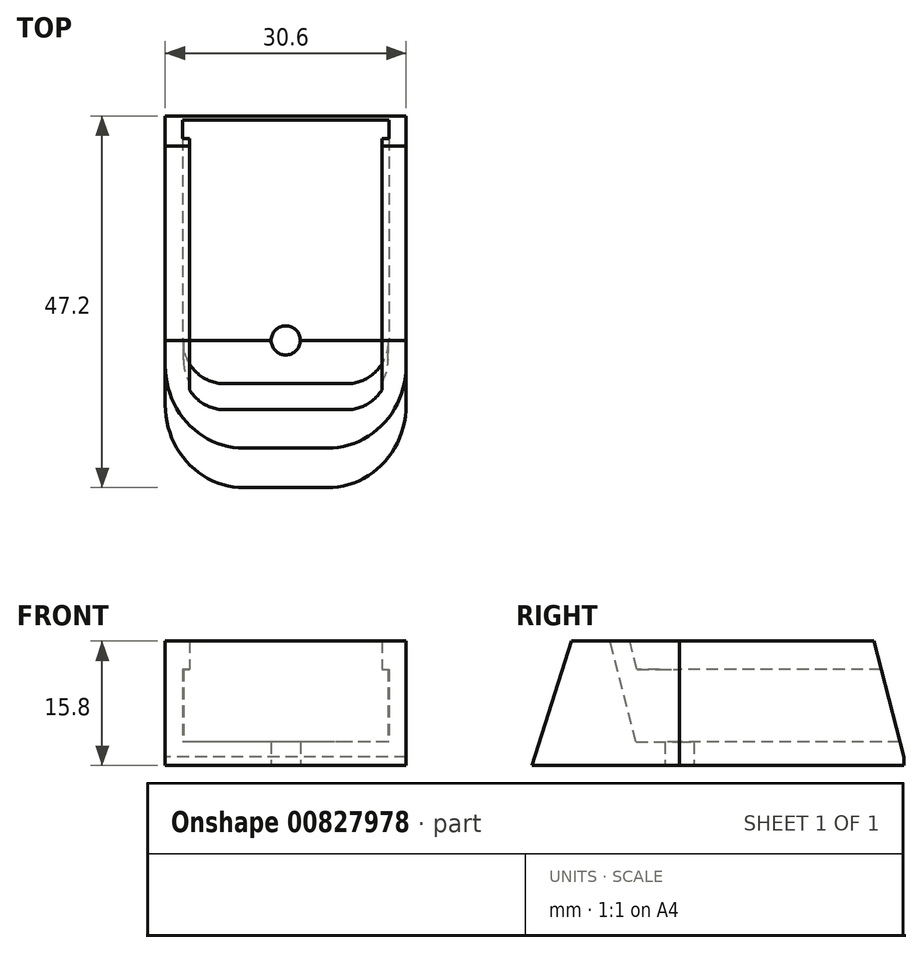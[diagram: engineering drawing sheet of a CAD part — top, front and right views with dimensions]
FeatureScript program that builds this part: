
annotation { "Feature Type Name" : "Feature", "Feature Type Description" : "" }
export const myFeature = defineFeature(function(context is Context, id is Id, definition is map)
    precondition{}
    {
        {
            var Q0;
            Q0=qCreatedBy(makeId("Front.planeOp"),FACE);
            var sketch = newSketch(context, id + "F0", { "sketchPlane" : qUnion([Q0])});
            skLineSegment(sketch, "E0", {"start": v(0, 0) * mm, "end": v(15.3, 0) * mm});
            skLineSegment(sketch, "E1", {"start": v(15.3, 0) * mm, "end": v(15.3, 15.8) * mm});
            skLineSegment(sketch, "E2", {"start": v(15.3, 15.8) * mm, "end": v(12.2, 15.8) * mm});
            skLineSegment(sketch, "E3", {"start": v(12.2, 15.8) * mm, "end": v(12.2, 12.2) * mm});
            skLineSegment(sketch, "E4", {"start": v(12.2, 12.2) * mm, "end": v(13.1, 12.2) * mm});
            skLineSegment(sketch, "E5", {"start": v(13.1, 12.2) * mm, "end": v(13.1, 3) * mm});
            skLineSegment(sketch, "E6", {"start": v(13.1, 3) * mm, "end": v(0, 3) * mm});
            skLineSegment(sketch, "E7", {"start": v(0, 0) * mm, "end": v(0, 34.13) * mm, "construction": true});
            skLineSegment(sketch, "E8.MirrorCS", {"start": v(-13.1, 3) * mm, "end": v(0, 3) * mm});
            skLineSegment(sketch, "E9.MirrorCS", {"start": v(0, 0) * mm, "end": v(-15.3, 0) * mm});
            skLineSegment(sketch, "E10.MirrorCS", {"start": v(-15.3, 0) * mm, "end": v(-15.3, 15.8) * mm});
            skLineSegment(sketch, "E11.MirrorCS", {"start": v(-13.1, 12.2) * mm, "end": v(-13.1, 3) * mm});
            skLineSegment(sketch, "E12.MirrorCS", {"start": v(-12.2, 12.2) * mm, "end": v(-13.1, 12.2) * mm});
            skLineSegment(sketch, "E13.MirrorCS", {"start": v(-15.3, 15.8) * mm, "end": v(-12.2, 15.8) * mm});
            skLineSegment(sketch, "E14.MirrorCS", {"start": v(-12.2, 15.8) * mm, "end": v(-12.2, 12.2) * mm});
            skSolve(sketch);
        }
        {
            var Q0;
            Q0=qCreatedBy(makeId("Right.planeOp"),FACE);
            var sketch = newSketch(context, id + "F1", { "sketchPlane" : qUnion([Q0])});
            skLineSegment(sketch, "E15", {"start": v(0, 0) * mm, "end": v(-18.7, 0) * mm});
            skLineSegment(sketch, "E16", {"start": v(-18.7, 0) * mm, "end": v(-13.7, 15.8) * mm});
            skLineSegment(sketch, "E17", {"start": v(-13.7, 15.8) * mm, "end": v(0, 15.8) * mm});
            skLineSegment(sketch, "E18", {"start": v(0, 15.8) * mm, "end": v(0, 0) * mm});
            skSolve(sketch);
        }
        {
            var Q0;
            Q0=qCreatedBy(makeId("Right.planeOp"),FACE);
            var sketch = newSketch(context, id + "F2", { "sketchPlane" : qUnion([Q0])});
            skLineSegment(sketch, "E19", {"start": v(0, 0) * mm, "end": v(0, 3) * mm, "construction": true});
            skLineSegment(sketch, "E20", {"start": v(0, 3) * mm, "end": v(-5.5, 3) * mm});
            skLineSegment(sketch, "E21", {"start": v(-5.5, 3) * mm, "end": v(-7.87, 12.2) * mm});
            skLineSegment(sketch, "E22", {"start": v(-7.87, 12.2) * mm, "end": v(25.63, 12.2) * mm});
            skLineSegment(sketch, "E23", {"start": v(25.63, 12.2) * mm, "end": v(28, 3) * mm});
            skLineSegment(sketch, "E24", {"start": v(28, 3) * mm, "end": v(0, 3) * mm});
            skLineSegment(sketch, "E25", {"start": v(-7.87, 12.2) * mm, "end": v(-8.8, 15.8) * mm});
            skLineSegment(sketch, "E26", {"start": v(-8.8, 15.8) * mm, "end": v(24.7, 15.8) * mm});
            skLineSegment(sketch, "E27", {"start": v(24.7, 15.8) * mm, "end": v(25.63, 12.2) * mm});
            skSolve(sketch);
        }
        {
            var Q0;
            Q0=makeQuery(id+"F2.imprint","IMPRINT",FACE,{"disambiguationData":[TD([[makeQuery(id+"F2.imprint","IMPRINT",EDGE,{"derivedFrom":sQuery(id+"F2.wireOp",EDGE,"E20")}),-1.0]])]});
            extrude(context, id + "F3", {"entities" : qUnion([Q0]), "endBound" : BoundingType.SYMMETRIC, "depth" : 26 * mm, "offsetDistance" : 25 * mm});
        }
        {
            var Q0;
            Q0=makeQuery(id+"F2.imprint","IMPRINT",FACE,{"disambiguationData":[TD([[makeQuery(id+"F2.imprint","IMPRINT",EDGE,{"derivedFrom":sQuery(id+"F2.wireOp",EDGE,"E22")}),1.0]])]});
            extrude(context, id + "F4", {"entities" : qUnion([Q0]), "operationType" : NewBodyOperationType.ADD, "endBound" : BoundingType.SYMMETRIC, "depth" : 24.4 * mm, "offsetDistance" : 25 * mm});
        }
        {
            var Q0;
            Q0=makeQuery(id+"F3.opExtrude","CAP_EDGE",EDGE,{"disambiguationData":[OSD([sQuery(id+"F2.wireOp",EDGE,"E21")])],"isStart":false});
            var Q1;
            Q1=makeQuery(id+"F3.opExtrude","CAP_EDGE",EDGE,{"disambiguationData":[OSD([sQuery(id+"F2.wireOp",EDGE,"E21")])],"isStart":true});
            fillet(context, id + "F5", {"entities" : qUnion([Q0, Q1]), "radius" : 5.2 * mm, "tangentPropagation" : true, "allowEdgeOverflow" : false});
        }
        {
            var Q0;
            Q0=makeQuery(id+"F1.imprint","IMPRINT",FACE,{"disambiguationData":[TD([[makeQuery(id+"F1.imprint","IMPRINT",EDGE,{"derivedFrom":sQuery(id+"F1.wireOp",EDGE,"E15")}),-1.0]])]});
            extrude(context, id + "F6", {"entities" : qUnion([Q0]), "endBound" : BoundingType.SYMMETRIC, "depth" : 30.6 * mm, "offsetDistance" : 25 * mm});
        }
        {
            var Q0;
            Q0=makeQuery(id+"F6.opExtrude","CAP_EDGE",EDGE,{"disambiguationData":[OSD([sQuery(id+"F1.wireOp",EDGE,"E16")])],"isStart":false});
            var Q1;
            Q1=makeQuery(id+"F6.opExtrude","CAP_EDGE",EDGE,{"disambiguationData":[OSD([sQuery(id+"F1.wireOp",EDGE,"E16")])],"isStart":true});
            fillet(context, id + "F7", {"entities" : qUnion([Q0, Q1]), "radius" : 10 * mm, "tangentPropagation" : true, "allowEdgeOverflow" : false});
        }
        {
            var Q0;
            Q0=makeQuery(id+"F0.imprint","IMPRINT",FACE,{"disambiguationData":[TD([[makeQuery(id+"F0.imprint","IMPRINT",EDGE,{"derivedFrom":sQuery(id+"F0.wireOp",EDGE,"E0")}),1.0]])]});
            extrude(context, id + "F8", {"entities" : qUnion([Q0]), "oppositeDirection" : true, "depth" : 28.5 * mm, "offsetDistance" : 25 * mm});
        }
        {
            var Q0;
            Q0=makeQuery(id+"F3.opExtrude","SWEPT_BODY",BODY,{"disambiguationData":[OSD([sQuery(id+"F2.wireOp",EDGE,"E20"),sQuery(id+"F2.wireOp",EDGE,"E21"),sQuery(id+"F2.wireOp",EDGE,"E22"),sQuery(id+"F2.wireOp",EDGE,"E23"),sQuery(id+"F2.wireOp",EDGE,"E24")])]});
            var Q1;
            Q1=makeQuery(id+"F6.opExtrude","SWEPT_BODY",BODY,{"disambiguationData":[OSD([sQuery(id+"F1.wireOp",EDGE,"E15"),sQuery(id+"F1.wireOp",EDGE,"E16"),sQuery(id+"F1.wireOp",EDGE,"E17"),sQuery(id+"F1.wireOp",EDGE,"E18")])]});
            var Q2;
            Q2=makeQuery(id+"F8.opExtrude","SWEPT_BODY",BODY,{"disambiguationData":[OSD([sQuery(id+"F0.wireOp",EDGE,"E0"),sQuery(id+"F0.wireOp",EDGE,"E1"),sQuery(id+"F0.wireOp",EDGE,"E2"),sQuery(id+"F0.wireOp",EDGE,"E3"),sQuery(id+"F0.wireOp",EDGE,"E4"),sQuery(id+"F0.wireOp",EDGE,"E5"),sQuery(id+"F0.wireOp",EDGE,"E6"),sQuery(id+"F0.wireOp",EDGE,"E8.MirrorCS"),sQuery(id+"F0.wireOp",EDGE,"E9.MirrorCS"),sQuery(id+"F0.wireOp",EDGE,"E10.MirrorCS"),sQuery(id+"F0.wireOp",EDGE,"E11.MirrorCS"),sQuery(id+"F0.wireOp",EDGE,"E12.MirrorCS"),sQuery(id+"F0.wireOp",EDGE,"E13.MirrorCS"),sQuery(id+"F0.wireOp",EDGE,"E14.MirrorCS")])]});
            booleanBodies(context, id + "F9", {"operationType" : BooleanOperationType.SUBTRACTION, "tools" : qUnion([Q0]), "targets" : qUnion([Q1, Q2])});
        }
        {
            var Q0;
            Q0=qCreatedBy(makeId("Top.planeOp"),FACE);
            var sketch = newSketch(context, id + "F10", { "sketchPlane" : qUnion([Q0])});
            skCircle(sketch, "E28", {"center": v(0, 0) * mm, "radius": 1.85 * mm});
            skSolve(sketch);
        }
        {
            var Q0;
            Q0=makeQuery(id+"F10.imprint","IMPRINT",FACE,{"disambiguationData":[TD([[makeQuery(id+"F10.imprint","IMPRINT",EDGE,{"derivedFrom":sQuery(id+"F10.wireOp",EDGE,"E28")}),1.0]])]});
            extrude(context, id + "F11", {"entities" : qUnion([Q0]), "depth" : 5 * mm, "offsetDistance" : 25 * mm});
        }
        {
            var Q0;
            Q0=makeQuery(id+"F11.opExtrude","SWEPT_BODY",BODY,{"disambiguationData":[OSD([sQuery(id+"F10.wireOp",EDGE,"E28")])]});
            var Q1;
            Q1=makeQuery(id+"F6.opExtrude","SWEPT_BODY",BODY,{"disambiguationData":[OSD([sQuery(id+"F1.wireOp",EDGE,"E15"),sQuery(id+"F1.wireOp",EDGE,"E16"),sQuery(id+"F1.wireOp",EDGE,"E17"),sQuery(id+"F1.wireOp",EDGE,"E18")])]});
            var Q2;
            Q2=makeQuery(id+"F8.opExtrude","SWEPT_BODY",BODY,{"disambiguationData":[OSD([sQuery(id+"F0.wireOp",EDGE,"E0"),sQuery(id+"F0.wireOp",EDGE,"E1"),sQuery(id+"F0.wireOp",EDGE,"E2"),sQuery(id+"F0.wireOp",EDGE,"E3"),sQuery(id+"F0.wireOp",EDGE,"E4"),sQuery(id+"F0.wireOp",EDGE,"E5"),sQuery(id+"F0.wireOp",EDGE,"E6"),sQuery(id+"F0.wireOp",EDGE,"E8.MirrorCS"),sQuery(id+"F0.wireOp",EDGE,"E9.MirrorCS"),sQuery(id+"F0.wireOp",EDGE,"E10.MirrorCS"),sQuery(id+"F0.wireOp",EDGE,"E11.MirrorCS"),sQuery(id+"F0.wireOp",EDGE,"E12.MirrorCS"),sQuery(id+"F0.wireOp",EDGE,"E13.MirrorCS"),sQuery(id+"F0.wireOp",EDGE,"E14.MirrorCS")])]});
            booleanBodies(context, id + "F12", {"operationType" : BooleanOperationType.SUBTRACTION, "tools" : qUnion([Q0]), "targets" : qUnion([Q1, Q2])});
        }
        {
            var Q0;
            Q0=qCreatedBy(makeId("Right.planeOp"),FACE);
            var sketch = newSketch(context, id + "F13", { "sketchPlane" : qUnion([Q0])});
            skPoint(sketch, "E29", {"position": v(28, 3) * mm});
            skPoint(sketch, "E30", {"position": v(24.7, 15.8) * mm});
            skLineSegment(sketch, "E31", {"start": v(24.7, 15.8) * mm, "end": v(28, 3) * mm});
            skLineSegment(sketch, "E32", {"start": v(28, 3) * mm, "end": v(29.3, -2.08) * mm});
            skLineSegment(sketch, "E33", {"start": v(29.3, -2.08) * mm, "end": v(29.3, 15.8) * mm});
            skLineSegment(sketch, "E34", {"start": v(29.3, 15.8) * mm, "end": v(24.7, 15.8) * mm});
            skSolve(sketch);
        }
        {
            var Q0;
            Q0=makeQuery(id+"F13.imprint","IMPRINT",FACE,{"disambiguationData":[TD([[makeQuery(id+"F13.imprint","IMPRINT",EDGE,{"derivedFrom":sQuery(id+"F13.wireOp",EDGE,"E31")}),1.0]])]});
            extrude(context, id + "F14", {"entities" : qUnion([Q0]), "operationType" : NewBodyOperationType.REMOVE, "endBound" : BoundingType.SYMMETRIC, "depth" : 40 * mm, "offsetDistance" : 25 * mm});
        }
    });
